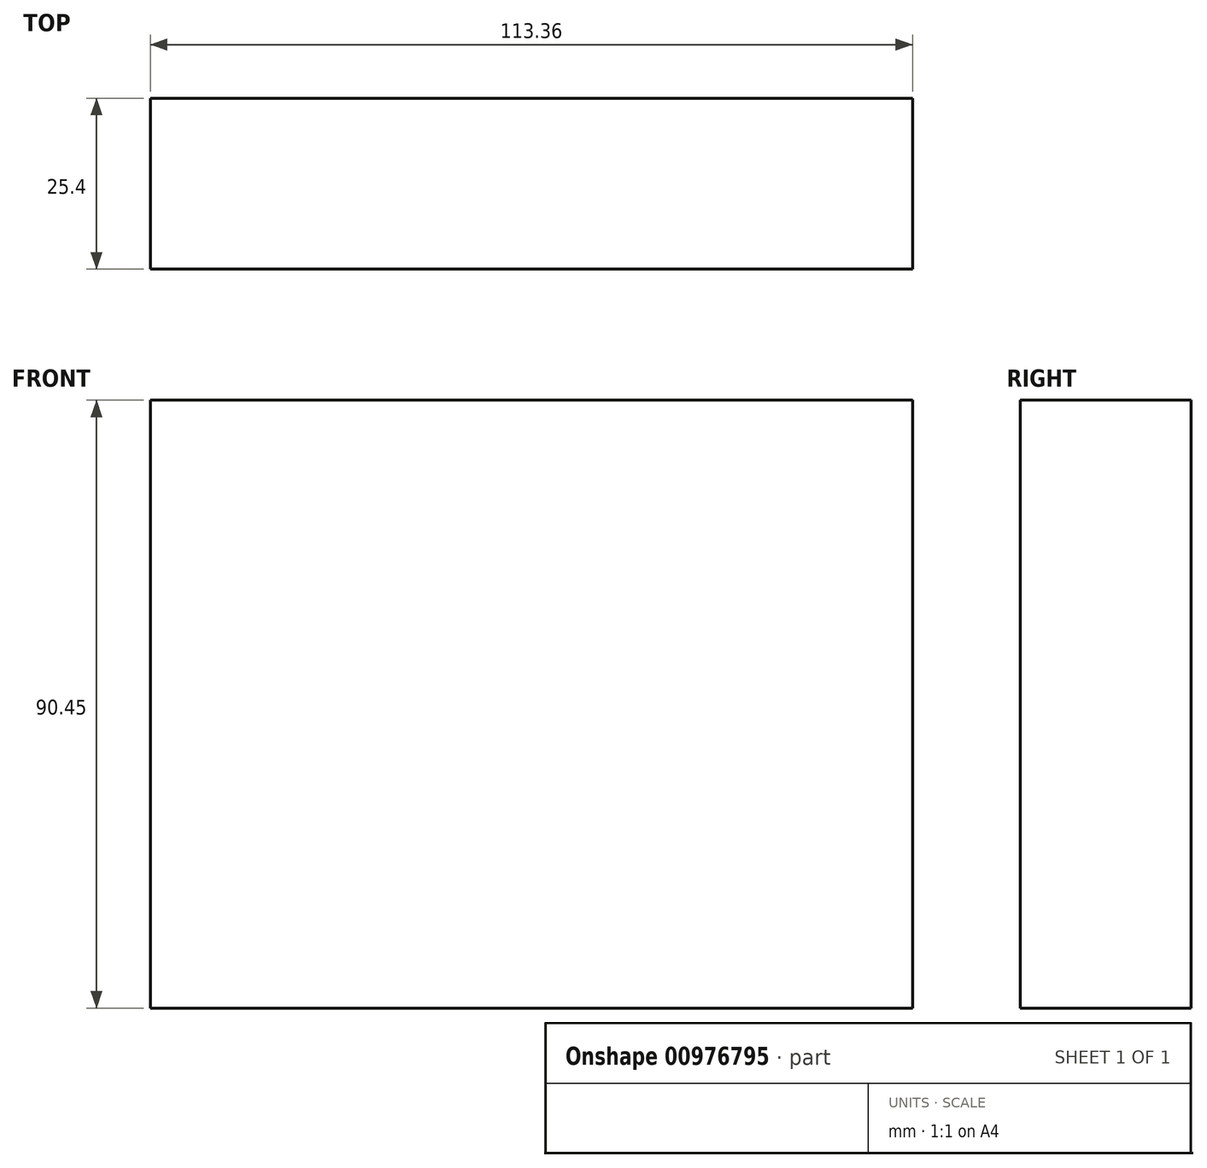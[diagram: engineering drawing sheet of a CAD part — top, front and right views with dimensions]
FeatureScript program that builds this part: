
annotation { "Feature Type Name" : "Feature", "Feature Type Description" : "" }
export const myFeature = defineFeature(function(context is Context, id is Id, definition is map)
    precondition{}
    {
        {
            var Q0;
            Q0=qCreatedBy(makeId("Front.planeOp"),FACE);
            var sketch = newSketch(context, id + "F0", { "sketchPlane" : qUnion([Q0])});
            skLineSegment(sketch, "E0.bottom", {"start": v(-121, -18.36) * mm, "end": v(-7.64, -18.36) * mm});
            skLineSegment(sketch, "E0.top", {"start": v(-121, -108.81) * mm, "end": v(-7.64, -108.81) * mm});
            skLineSegment(sketch, "E0.left", {"start": v(-121, -18.36) * mm, "end": v(-121, -108.81) * mm});
            skLineSegment(sketch, "E0.right", {"start": v(-7.64, -18.36) * mm, "end": v(-7.64, -108.81) * mm});
            skSolve(sketch);
        }
        {
            var Q0;
            Q0 = qSketchRegion(id + "F0", true);
            extrude(context, id + "F1", {"entities" : qUnion([Q0]), "depth" : 25.4 * mm, "offsetDistance" : 25.4 * mm});
        }
    });
